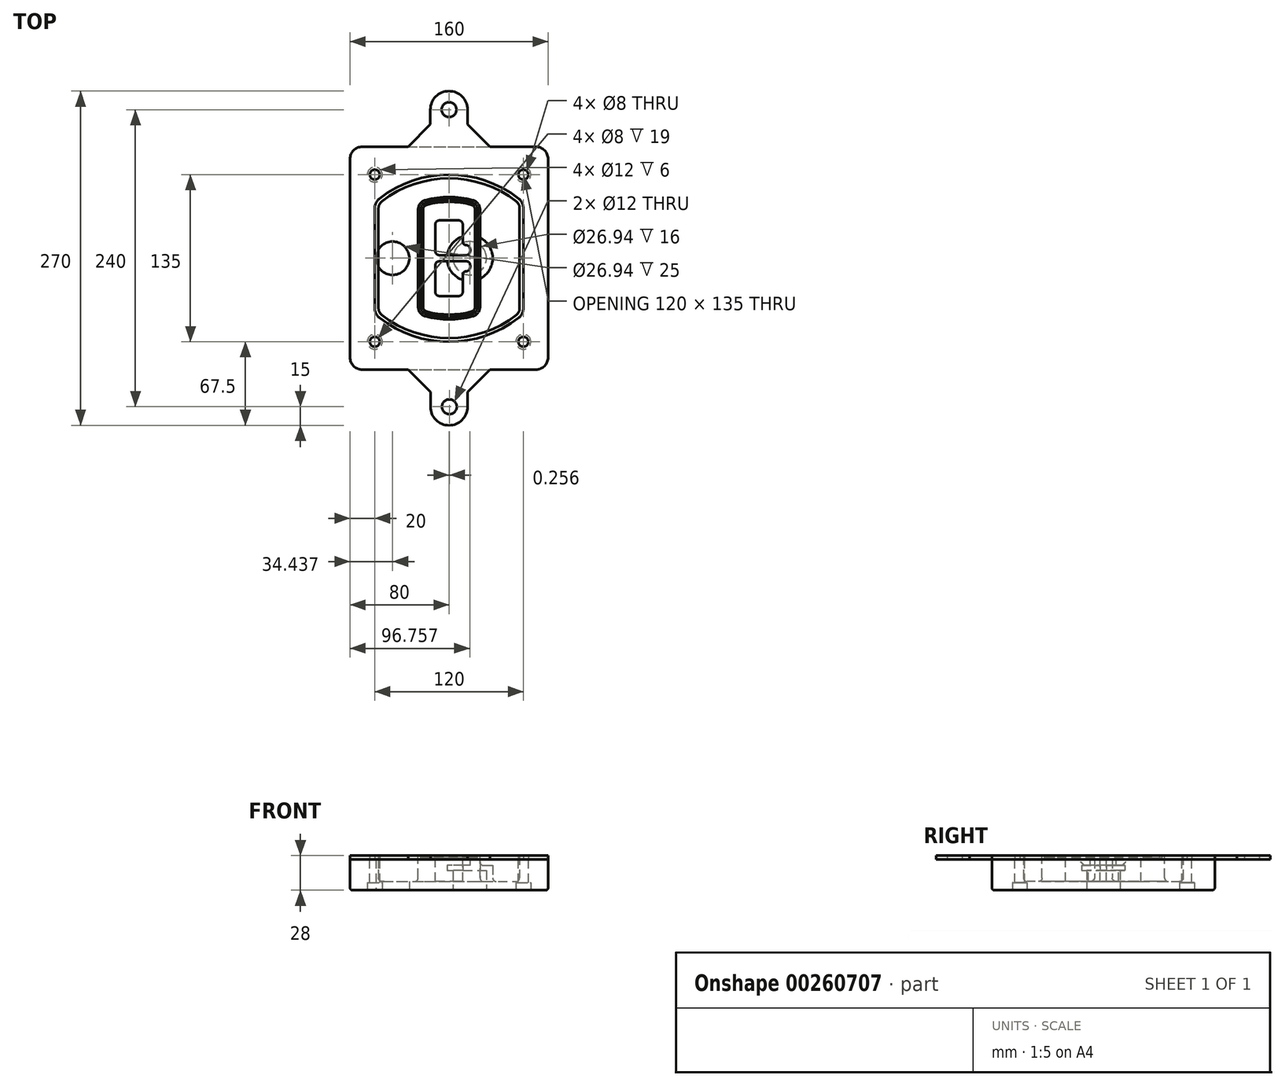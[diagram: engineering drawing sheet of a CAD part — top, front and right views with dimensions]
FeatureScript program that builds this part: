
annotation { "Feature Type Name" : "Feature", "Feature Type Description" : "" }
export const myFeature = defineFeature(function(context is Context, id is Id, definition is map)
    precondition{}
    {
        {
            var Q0;
            Q0=qCreatedBy(makeId("Top.planeOp"),FACE);
            var sketch = newSketch(context, id + "F0", { "sketchPlane" : qUnion([Q0])});
            skPoint(sketch, "E0.rect.middle", {"position": v(0, 0) * mm});
            skLineSegment(sketch, "E1.bottom", {"start": v(-70, -90) * mm, "end": v(70, -90) * mm});
            skLineSegment(sketch, "E1.top", {"start": v(-70, 90) * mm, "end": v(70, 90) * mm});
            skLineSegment(sketch, "E1.left", {"start": v(-80, -80) * mm, "end": v(-80, 80) * mm});
            skLineSegment(sketch, "E1.right", {"start": v(80, -80) * mm, "end": v(80, 80) * mm});
            skLineSegment(sketch, "E2", {"start": v(-80, 90) * mm, "end": v(80, -90) * mm, "construction": true});
            skLineSegment(sketch, "E3", {"start": v(80, 90) * mm, "end": v(-80, -90) * mm, "construction": true});
            skCircle(sketch, "E4", {"center": v(-60, 67.5) * mm, "radius": 4 * mm});
            skCircle(sketch, "E5", {"center": v(60, 67.5) * mm, "radius": 4 * mm});
            skCircle(sketch, "E6", {"center": v(60, -67.5) * mm, "radius": 4 * mm});
            skCircle(sketch, "E7", {"center": v(-60, -67.5) * mm, "radius": 4 * mm});
            skLineSegment(sketch, "E8", {"start": v(-60, 67.5) * mm, "end": v(60, 67.5) * mm, "construction": true});
            skLineSegment(sketch, "E9", {"start": v(60, 67.5) * mm, "end": v(60, -67.5) * mm, "construction": true});
            skLineSegment(sketch, "E10", {"start": v(60, -67.5) * mm, "end": v(-60, -67.5) * mm, "construction": true});
            skLineSegment(sketch, "E11", {"start": v(-60, -67.5) * mm, "end": v(-60, 67.5) * mm, "construction": true});
            skLineSegment(sketch, "E12", {"start": v(-60, 40.3) * mm, "end": v(-60, -40.3) * mm});
            skLineSegment(sketch, "E13", {"start": v(60, 40.3) * mm, "end": v(60, -40.3) * mm});
            skArc(sketch, "E14", {"start": v(56.15, 48.18) * mm, "mid": v(0, 67.5) * mm, "end": v(-56.15, 48.18) * mm});
            skArc(sketch, "E15", {"start": v(-56.15, -48.18) * mm, "mid": v(0, -67.5) * mm, "end": v(56.15, -48.18) * mm});
            skLineSegment(sketch, "E16", {"start": v(-60, 0) * mm, "end": v(60, 0) * mm, "construction": true});
            skPoint(sketch, "E17.visualSharp", {"position": v(-60, -45) * mm});
            skArc(sketch, "E17.filletArc", {"start": v(-60, -40.3) * mm, "mid": v(-58.99, -44.68) * mm, "end": v(-56.15, -48.18) * mm});
            skPoint(sketch, "E18.visualSharp", {"position": v(-60, 45) * mm});
            skArc(sketch, "E18.filletArc", {"start": v(-56.15, 48.18) * mm, "mid": v(-58.99, 44.68) * mm, "end": v(-60, 40.3) * mm});
            skPoint(sketch, "E19.visualSharp", {"position": v(60, 45) * mm});
            skArc(sketch, "E19.filletArc", {"start": v(60, 40.3) * mm, "mid": v(58.99, 44.68) * mm, "end": v(56.15, 48.18) * mm});
            skPoint(sketch, "E20.visualSharp", {"position": v(60, -45) * mm});
            skArc(sketch, "E20.filletArc", {"start": v(56.15, -48.18) * mm, "mid": v(58.99, -44.68) * mm, "end": v(60, -40.3) * mm});
            skPoint(sketch, "E21.visualSharp", {"position": v(-80, 90) * mm});
            skArc(sketch, "E21.filletArc", {"start": v(-70, 90) * mm, "mid": v(-77.07, 87.07) * mm, "end": v(-80, 80) * mm});
            skPoint(sketch, "E22.visualSharp", {"position": v(80, 90) * mm});
            skArc(sketch, "E22.filletArc", {"start": v(80, 80) * mm, "mid": v(77.07, 87.07) * mm, "end": v(70, 90) * mm});
            skPoint(sketch, "E23.visualSharp", {"position": v(80, -90) * mm});
            skArc(sketch, "E23.filletArc", {"start": v(70, -90) * mm, "mid": v(77.07, -87.07) * mm, "end": v(80, -80) * mm});
            skPoint(sketch, "E24.visualSharp", {"position": v(-80, -90) * mm});
            skArc(sketch, "E24.filletArc", {"start": v(-80, -80) * mm, "mid": v(-77.07, -87.07) * mm, "end": v(-70, -90) * mm});
            skArc(sketch, "E25.0", {"start": v(57, 40.3) * mm, "mid": v(56.3, 43.36) * mm, "end": v(54.3, 45.81) * mm});
            skLineSegment(sketch, "E25.1", {"start": v(57, 40.3) * mm, "end": v(57, -40.3) * mm});
            skArc(sketch, "E25.2", {"start": v(54.3, -45.81) * mm, "mid": v(56.3, -43.36) * mm, "end": v(57, -40.3) * mm});
            skArc(sketch, "E25.3", {"start": v(-54.3, -45.81) * mm, "mid": v(0, -64.5) * mm, "end": v(54.3, -45.81) * mm});
            skArc(sketch, "E25.4", {"start": v(-57, -40.3) * mm, "mid": v(-56.3, -43.36) * mm, "end": v(-54.3, -45.81) * mm});
            skArc(sketch, "E25.5", {"start": v(54.3, 45.81) * mm, "mid": v(0, 64.5) * mm, "end": v(-54.3, 45.81) * mm});
            skLineSegment(sketch, "E25.6", {"start": v(-57, 40.3) * mm, "end": v(-57, -40.3) * mm});
            skArc(sketch, "E25.7", {"start": v(-54.3, 45.81) * mm, "mid": v(-56.3, 43.36) * mm, "end": v(-57, 40.3) * mm});
            skArc(sketch, "E26.0", {"start": v(-58.62, 51.33) * mm, "mid": v(-62.58, 46.43) * mm, "end": v(-64, 40.3) * mm});
            skArc(sketch, "E26.1", {"start": v(58.62, 51.33) * mm, "mid": v(0, 71.5) * mm, "end": v(-58.62, 51.33) * mm});
            skArc(sketch, "E26.2", {"start": v(64, 40.3) * mm, "mid": v(62.58, 46.43) * mm, "end": v(58.62, 51.33) * mm});
            skLineSegment(sketch, "E26.3", {"start": v(64, 40.3) * mm, "end": v(64, -40.3) * mm});
            skArc(sketch, "E26.4", {"start": v(58.62, -51.33) * mm, "mid": v(62.58, -46.43) * mm, "end": v(64, -40.3) * mm});
            skLineSegment(sketch, "E26.5", {"start": v(-64, 40.3) * mm, "end": v(-64, -40.3) * mm});
            skArc(sketch, "E26.6", {"start": v(-58.62, -51.33) * mm, "mid": v(0, -71.5) * mm, "end": v(58.62, -51.33) * mm});
            skArc(sketch, "E26.7", {"start": v(-64, -40.3) * mm, "mid": v(-62.58, -46.43) * mm, "end": v(-58.62, -51.33) * mm});
            skSolve(sketch);
        }
        {
            var Q0;
            Q0=makeQuery(id+"F0.imprint","IMPRINT",FACE,{"disambiguationData":[TD([[makeQuery(id+"F0.imprint","IMPRINT",EDGE,{"derivedFrom":sQuery(id+"F0.wireOp",EDGE,"E1.bottom")}),1.0]])]});
            var Q1;
            Q1=makeQuery(id+"F0.imprint","IMPRINT",FACE,{"disambiguationData":[TD([[makeQuery(id+"F0.imprint","IMPRINT",EDGE,{"derivedFrom":sQuery(id+"F0.wireOp",EDGE,"E12")}),1.0]])]});
            var Q2;
            Q2=makeQuery(id+"F0.imprint","IMPRINT",FACE,{"disambiguationData":[TD([[makeQuery(id+"F0.imprint","IMPRINT",EDGE,{"derivedFrom":sQuery(id+"F0.wireOp",EDGE,"E25.0")}),1.0]])]});
            var Q3;
            Q3=makeQuery(id+"F0.imprint","IMPRINT",FACE,{"disambiguationData":[TD([[makeQuery(id+"F0.imprint","IMPRINT",EDGE,{"derivedFrom":sQuery(id+"F0.wireOp",EDGE,"E12")}),-1.0]])]});
            extrude(context, id + "F1", {"entities" : qUnion([Q0, Q1, Q2, Q3]), "oppositeDirection" : true, "depth" : 25 * mm});
        }
        {
            var Q0;
            Q0=makeQuery(id+"F0.imprint","IMPRINT",FACE,{"disambiguationData":[TD([[makeQuery(id+"F0.imprint","IMPRINT",EDGE,{"derivedFrom":sQuery(id+"F0.wireOp",EDGE,"E12")}),1.0]])]});
            extrude(context, id + "F2", {"entities" : qUnion([Q0]), "operationType" : NewBodyOperationType.ADD, "depth" : 3 * mm});
        }
        {
            var Q0;
            Q0=makeQuery(id+"F0.imprint","IMPRINT",FACE,{"disambiguationData":[TD([[makeQuery(id+"F0.imprint","IMPRINT",EDGE,{"derivedFrom":sQuery(id+"F0.wireOp",EDGE,"E25.0")}),1.0]])]});
            extrude(context, id + "F3", {"entities" : qUnion([Q0]), "operationType" : NewBodyOperationType.REMOVE, "oppositeDirection" : true, "depth" : 18 * mm});
        }
        {
            var Q0;
            Q0=makeQuery(id+"F2.opExtrude","CAP_FACE",FACE,{"disambiguationData":[OSD([sQuery(id+"F0.wireOp",EDGE,"E12"),sQuery(id+"F0.wireOp",EDGE,"E13"),sQuery(id+"F0.wireOp",EDGE,"E14"),sQuery(id+"F0.wireOp",EDGE,"E15"),sQuery(id+"F0.wireOp",EDGE,"E17.filletArc"),sQuery(id+"F0.wireOp",EDGE,"E18.filletArc"),sQuery(id+"F0.wireOp",EDGE,"E19.filletArc"),sQuery(id+"F0.wireOp",EDGE,"E20.filletArc"),sQuery(id+"F0.wireOp",EDGE,"E25.0"),sQuery(id+"F0.wireOp",EDGE,"E25.1"),sQuery(id+"F0.wireOp",EDGE,"E25.2"),sQuery(id+"F0.wireOp",EDGE,"E25.3"),sQuery(id+"F0.wireOp",EDGE,"E25.4"),sQuery(id+"F0.wireOp",EDGE,"E25.5"),sQuery(id+"F0.wireOp",EDGE,"E25.6"),sQuery(id+"F0.wireOp",EDGE,"E25.7")])],"isStart":false});
            var sketch = newSketch(context, id + "F4", { "sketchPlane" : qUnion([Q0])});
            skArc(sketch, "E27.0", {"start": v(-19.08, -46.97) * mm, "mid": v(0, -49.5) * mm, "end": v(19.08, -46.97) * mm});
            skArc(sketch, "E28.0", {"start": v(19.08, 46.97) * mm, "mid": v(0, 49.5) * mm, "end": v(-19.08, 46.97) * mm});
            skLineSegment(sketch, "E29", {"start": v(-25, 39.25) * mm, "end": v(-25, -39.25) * mm});
            skLineSegment(sketch, "E30", {"start": v(25, 39.25) * mm, "end": v(25, -39.25) * mm});
            skLineSegment(sketch, "E31", {"start": v(-25, 45.1) * mm, "end": v(25, 45.1) * mm, "construction": true});
            skLineSegment(sketch, "E32", {"start": v(-25, -45.1) * mm, "end": v(25, -45.1) * mm, "construction": true});
            skPoint(sketch, "E33.visualSharp", {"position": v(-25, 45.1) * mm});
            skArc(sketch, "E33.filletArc", {"start": v(-19.08, 46.97) * mm, "mid": v(-23.35, 44.11) * mm, "end": v(-25, 39.25) * mm});
            skPoint(sketch, "E34.visualSharp", {"position": v(25, 45.1) * mm});
            skArc(sketch, "E34.filletArc", {"start": v(25, 39.25) * mm, "mid": v(23.35, 44.11) * mm, "end": v(19.08, 46.97) * mm});
            skPoint(sketch, "E35.visualSharp", {"position": v(25, -45.1) * mm});
            skArc(sketch, "E35.filletArc", {"start": v(19.08, -46.97) * mm, "mid": v(23.35, -44.11) * mm, "end": v(25, -39.25) * mm});
            skPoint(sketch, "E36.visualSharp", {"position": v(-25, -45.1) * mm});
            skArc(sketch, "E36.filletArc", {"start": v(-25, -39.25) * mm, "mid": v(-23.35, -44.11) * mm, "end": v(-19.08, -46.97) * mm});
            skArc(sketch, "E37.0", {"start": v(54.3, 45.81) * mm, "mid": v(0, 64.5) * mm, "end": v(-54.3, 45.81) * mm});
            skArc(sketch, "E37.1", {"start": v(-54.3, 45.81) * mm, "mid": v(-56.3, 43.36) * mm, "end": v(-57, 40.3) * mm});
            skLineSegment(sketch, "E37.2", {"start": v(-57, 40.3) * mm, "end": v(-57, -40.3) * mm});
            skArc(sketch, "E37.3", {"start": v(-57, -40.3) * mm, "mid": v(-56.3, -43.36) * mm, "end": v(-54.3, -45.81) * mm});
            skArc(sketch, "E37.4", {"start": v(-54.3, -45.81) * mm, "mid": v(0, -64.5) * mm, "end": v(54.3, -45.81) * mm});
            skArc(sketch, "E37.5", {"start": v(54.3, -45.81) * mm, "mid": v(56.3, -43.36) * mm, "end": v(57, -40.3) * mm});
            skLineSegment(sketch, "E37.6", {"start": v(57, 40.3) * mm, "end": v(57, -40.3) * mm});
            skArc(sketch, "E37.7", {"start": v(57, 40.3) * mm, "mid": v(56.3, 43.36) * mm, "end": v(54.3, 45.81) * mm});
            skLineSegment(sketch, "E38.0", {"start": v(23, 39.25) * mm, "end": v(23, -39.25) * mm});
            skArc(sketch, "E38.1", {"start": v(18.56, -45.04) * mm, "mid": v(21.76, -42.9) * mm, "end": v(23, -39.25) * mm});
            skArc(sketch, "E38.2", {"start": v(-18.56, -45.04) * mm, "mid": v(0, -47.5) * mm, "end": v(18.56, -45.04) * mm});
            skArc(sketch, "E38.3", {"start": v(-23, -39.25) * mm, "mid": v(-21.76, -42.9) * mm, "end": v(-18.56, -45.04) * mm});
            skLineSegment(sketch, "E38.4", {"start": v(-23, 39.25) * mm, "end": v(-23, -39.25) * mm});
            skArc(sketch, "E38.5", {"start": v(23, 39.25) * mm, "mid": v(21.76, 42.9) * mm, "end": v(18.56, 45.04) * mm});
            skArc(sketch, "E38.6", {"start": v(-18.56, 45.04) * mm, "mid": v(-21.76, 42.9) * mm, "end": v(-23, 39.25) * mm});
            skArc(sketch, "E38.7", {"start": v(18.56, 45.04) * mm, "mid": v(0, 47.5) * mm, "end": v(-18.56, 45.04) * mm});
            skArc(sketch, "E39.0", {"start": v(21, 39.25) * mm, "mid": v(20.18, 41.68) * mm, "end": v(18.04, 43.1) * mm});
            skLineSegment(sketch, "E39.1", {"start": v(21, 39.25) * mm, "end": v(21, -39.25) * mm});
            skArc(sketch, "E39.2", {"start": v(18.04, -43.1) * mm, "mid": v(20.18, -41.68) * mm, "end": v(21, -39.25) * mm});
            skArc(sketch, "E39.3", {"start": v(-18.04, -43.1) * mm, "mid": v(0, -45.5) * mm, "end": v(18.04, -43.1) * mm});
            skArc(sketch, "E39.4", {"start": v(-21, -39.25) * mm, "mid": v(-20.18, -41.68) * mm, "end": v(-18.04, -43.1) * mm});
            skArc(sketch, "E39.5", {"start": v(18.04, 43.1) * mm, "mid": v(0, 45.5) * mm, "end": v(-18.04, 43.1) * mm});
            skLineSegment(sketch, "E39.6", {"start": v(-21, 39.25) * mm, "end": v(-21, -39.25) * mm});
            skArc(sketch, "E39.7", {"start": v(-18.04, 43.1) * mm, "mid": v(-20.18, 41.68) * mm, "end": v(-21, 39.25) * mm});
            skLineSegment(sketch, "E40", {"start": v(-25, 0) * mm, "end": v(25, 0) * mm, "construction": true});
            skLineSegment(sketch, "E41", {"start": v(-11, 5.5) * mm, "end": v(-11, 27.5) * mm});
            skLineSegment(sketch, "E42", {"start": v(-8, 30.5) * mm, "end": v(8, 30.5) * mm});
            skLineSegment(sketch, "E43", {"start": v(11, 27.5) * mm, "end": v(11, 13.5) * mm});
            skLineSegment(sketch, "E44", {"start": v(14, 10.5) * mm, "end": v(14, 10.5) * mm});
            skLineSegment(sketch, "E45", {"start": v(17, 7.5) * mm, "end": v(17, 5.5) * mm});
            skLineSegment(sketch, "E46", {"start": v(14, 2.5) * mm, "end": v(-8, 2.5) * mm});
            skPoint(sketch, "E47.visualSharp", {"position": v(-11, 30.5) * mm});
            skArc(sketch, "E47.filletArc", {"start": v(-8, 30.5) * mm, "mid": v(-10.12, 29.62) * mm, "end": v(-11, 27.5) * mm});
            skPoint(sketch, "E48.visualSharp", {"position": v(11, 30.5) * mm});
            skArc(sketch, "E48.filletArc", {"start": v(11, 27.5) * mm, "mid": v(10.12, 29.62) * mm, "end": v(8, 30.5) * mm});
            skPoint(sketch, "E49.visualSharp", {"position": v(11, 10.5) * mm});
            skArc(sketch, "E49.filletArc", {"start": v(11, 13.5) * mm, "mid": v(11.88, 11.38) * mm, "end": v(14, 10.5) * mm});
            skPoint(sketch, "E50.visualSharp", {"position": v(17, 10.5) * mm});
            skArc(sketch, "E50.filletArc", {"start": v(17, 7.5) * mm, "mid": v(16.12, 9.62) * mm, "end": v(14, 10.5) * mm});
            skPoint(sketch, "E51.visualSharp", {"position": v(17, 2.5) * mm});
            skArc(sketch, "E51.filletArc", {"start": v(14, 2.5) * mm, "mid": v(16.12, 3.38) * mm, "end": v(17, 5.5) * mm});
            skPoint(sketch, "E52.visualSharp", {"position": v(-11, 2.5) * mm});
            skArc(sketch, "E52.filletArc", {"start": v(-11, 5.5) * mm, "mid": v(-10.12, 3.38) * mm, "end": v(-8, 2.5) * mm});
            skLineSegment(sketch, "E53.0.MirrorCS", {"start": v(14, -2.5) * mm, "end": v(-8, -2.5) * mm});
            skArc(sketch, "E54.0.MirrorCS", {"start": v(-11, -5.5) * mm, "mid": v(-10.12, -3.38) * mm, "end": v(-8, -2.5) * mm});
            skLineSegment(sketch, "E55.0.MirrorCS", {"start": v(-11, -5.5) * mm, "end": v(-11, -27.5) * mm});
            skArc(sketch, "E56.0.MirrorCS", {"start": v(-8, -30.5) * mm, "mid": v(-10.12, -29.62) * mm, "end": v(-11, -27.5) * mm});
            skLineSegment(sketch, "E57.0.MirrorCS", {"start": v(-8, -30.5) * mm, "end": v(8, -30.5) * mm});
            skArc(sketch, "E58.0.MirrorCS", {"start": v(11, -27.5) * mm, "mid": v(10.12, -29.62) * mm, "end": v(8, -30.5) * mm});
            skLineSegment(sketch, "E59.0.MirrorCS", {"start": v(11, -27.5) * mm, "end": v(11, -13.5) * mm});
            skArc(sketch, "E60.0.MirrorCS", {"start": v(11, -13.5) * mm, "mid": v(11.88, -11.38) * mm, "end": v(14, -10.5) * mm});
            skArc(sketch, "E61.0.MirrorCS", {"start": v(17, -7.5) * mm, "mid": v(16.12, -9.62) * mm, "end": v(14, -10.5) * mm});
            skLineSegment(sketch, "E62.0.MirrorCS", {"start": v(17, -7.5) * mm, "end": v(17, -5.5) * mm});
            skArc(sketch, "E63.0.MirrorCS", {"start": v(14, -2.5) * mm, "mid": v(16.12, -3.38) * mm, "end": v(17, -5.5) * mm});
            skSolve(sketch);
        }
        {
            var Q0;
            Q0=makeQuery(id+"F4.imprint","IMPRINT",FACE,{"disambiguationData":[TD([[makeQuery(id+"F4.imprint","IMPRINT",EDGE,{"derivedFrom":sQuery(id+"F4.wireOp",EDGE,"E27.0")}),1.0]])]});
            var Q1;
            Q1=makeQuery(id+"F4.imprint","IMPRINT",FACE,{"disambiguationData":[TD([[makeQuery(id+"F4.imprint","IMPRINT",EDGE,{"derivedFrom":sQuery(id+"F4.wireOp",EDGE,"E38.0")}),-1.0]])]});
            var Q2;
            Q2=makeQuery(id+"F4.imprint","IMPRINT",FACE,{"disambiguationData":[TD([[makeQuery(id+"F4.imprint","IMPRINT",EDGE,{"derivedFrom":sQuery(id+"F4.wireOp",EDGE,"E39.0")}),1.0]])]});
            extrude(context, id + "F5", {"entities" : qUnion([Q0, Q1, Q2]), "operationType" : NewBodyOperationType.ADD, "endBound" : BoundingType.UP_TO_NEXT, "oppositeDirection" : true, "depth" : 25 * mm});
        }
        {
            var Q0;
            Q0=makeQuery(id+"F4.imprint","IMPRINT",FACE,{"disambiguationData":[TD([[makeQuery(id+"F4.imprint","IMPRINT",EDGE,{"derivedFrom":sQuery(id+"F4.wireOp",EDGE,"E38.0")}),-1.0]])]});
            extrude(context, id + "F6", {"entities" : qUnion([Q0]), "operationType" : NewBodyOperationType.REMOVE, "oppositeDirection" : true, "depth" : 2 * mm});
        }
        {
            var Q0;
            Q0=makeQuery(id+"F1.opExtrude","CAP_FACE",FACE,{"disambiguationData":[OSD([sQuery(id+"F0.wireOp",EDGE,"E1.bottom"),sQuery(id+"F0.wireOp",EDGE,"E1.top"),sQuery(id+"F0.wireOp",EDGE,"E1.left"),sQuery(id+"F0.wireOp",EDGE,"E1.right"),sQuery(id+"F0.wireOp",EDGE,"E4"),sQuery(id+"F0.wireOp",EDGE,"E5"),sQuery(id+"F0.wireOp",EDGE,"E6"),sQuery(id+"F0.wireOp",EDGE,"E7"),sQuery(id+"F0.wireOp",EDGE,"E21.filletArc"),sQuery(id+"F0.wireOp",EDGE,"E22.filletArc"),sQuery(id+"F0.wireOp",EDGE,"E23.filletArc"),sQuery(id+"F0.wireOp",EDGE,"E24.filletArc")])],"isStart":false});
            var sketch = newSketch(context, id + "F7", { "sketchPlane" : qUnion([Q0])});
            skCircle(sketch, "E64", {"center": v(16.76, 0) * mm, "radius": 13.47 * mm});
            skCircle(sketch, "E65", {"center": v(-45.56, 0) * mm, "radius": 13.47 * mm});
            skLineSegment(sketch, "E66", {"start": v(80, 0) * mm, "end": v(-80, 0) * mm});
            skCircle(sketch, "E67", {"center": v(16.76, 0) * mm, "radius": 18.47 * mm});
            skCircle(sketch, "E68", {"center": v(60, -67.5) * mm, "radius": 6 * mm});
            skCircle(sketch, "E69", {"center": v(-60, -67.5) * mm, "radius": 6 * mm});
            skCircle(sketch, "E70", {"center": v(-60, 67.5) * mm, "radius": 6 * mm});
            skCircle(sketch, "E71", {"center": v(60, 67.5) * mm, "radius": 6 * mm});
            skSolve(sketch);
        }
        {
            var Q0;
            {var subQ1=sQuery(id+"F7.wireOp",EDGE,"E66");var subQ4=sQuery(id+"F7.wireOp",EDGE,"E64");var subQ6=makeQuery(id+"F7.imprint","INTERSECT",VERTEX,{"disambiguationData":[OD(0.0)],"derivedFrom":[subQ4,subQ1]});Q0=makeQuery(id+"F7.imprint","IMPRINT",FACE,{"disambiguationData":[TD([[makeQuery(id+"F7.imprint","IMPRINT",EDGE,{"disambiguationData":[TD([[subQ6,-1.0]])],"derivedFrom":subQ4}),-1.0]])]});}
            var Q1;
            {var subQ0=sQuery(id+"F7.wireOp",EDGE,"E66");var subQ1=sQuery(id+"F7.wireOp",EDGE,"E64");var subQ3=makeQuery(id+"F7.imprint","INTERSECT",VERTEX,{"disambiguationData":[OD(0.0)],"derivedFrom":[subQ1,subQ0]});Q1=makeQuery(id+"F7.imprint","IMPRINT",FACE,{"disambiguationData":[TD([[makeQuery(id+"F7.imprint","IMPRINT",EDGE,{"disambiguationData":[TD([[subQ3,-1.0]])],"derivedFrom":subQ1}),1.0]])]});}
            var Q2;
            {var subQ0=sQuery(id+"F7.wireOp",EDGE,"E66");var subQ1=sQuery(id+"F7.wireOp",EDGE,"E64");var subQ3=makeQuery(id+"F7.imprint","INTERSECT",VERTEX,{"disambiguationData":[OD(0.0)],"derivedFrom":[subQ1,subQ0]});Q2=makeQuery(id+"F7.imprint","IMPRINT",FACE,{"disambiguationData":[TD([[makeQuery(id+"F7.imprint","IMPRINT",EDGE,{"disambiguationData":[TD([[subQ3,1.0]])],"derivedFrom":subQ1}),1.0]])]});}
            var Q3;
            {var subQ1=sQuery(id+"F7.wireOp",EDGE,"E66");var subQ4=sQuery(id+"F7.wireOp",EDGE,"E64");var subQ6=makeQuery(id+"F7.imprint","INTERSECT",VERTEX,{"disambiguationData":[OD(0.0)],"derivedFrom":[subQ4,subQ1]});Q3=makeQuery(id+"F7.imprint","IMPRINT",FACE,{"disambiguationData":[TD([[makeQuery(id+"F7.imprint","IMPRINT",EDGE,{"disambiguationData":[TD([[subQ6,1.0]])],"derivedFrom":subQ4}),-1.0]])]});}
            extrude(context, id + "F8", {"entities" : qUnion([Q0, Q1, Q2, Q3]), "operationType" : NewBodyOperationType.ADD, "oppositeDirection" : true, "depth" : 20 * mm});
        }
        {
            var Q0;
            {var subQ0=sQuery(id+"F7.wireOp",EDGE,"E66");var subQ1=sQuery(id+"F7.wireOp",EDGE,"E64");var subQ3=makeQuery(id+"F7.imprint","INTERSECT",VERTEX,{"disambiguationData":[OD(0.0)],"derivedFrom":[subQ1,subQ0]});Q0=makeQuery(id+"F7.imprint","IMPRINT",FACE,{"disambiguationData":[TD([[makeQuery(id+"F7.imprint","IMPRINT",EDGE,{"disambiguationData":[TD([[subQ3,-1.0]])],"derivedFrom":subQ1}),1.0]])]});}
            var Q1;
            {var subQ0=sQuery(id+"F7.wireOp",EDGE,"E66");var subQ1=sQuery(id+"F7.wireOp",EDGE,"E64");var subQ3=makeQuery(id+"F7.imprint","INTERSECT",VERTEX,{"disambiguationData":[OD(0.0)],"derivedFrom":[subQ1,subQ0]});Q1=makeQuery(id+"F7.imprint","IMPRINT",FACE,{"disambiguationData":[TD([[makeQuery(id+"F7.imprint","IMPRINT",EDGE,{"disambiguationData":[TD([[subQ3,1.0]])],"derivedFrom":subQ1}),1.0]])]});}
            extrude(context, id + "F9", {"entities" : qUnion([Q0, Q1]), "operationType" : NewBodyOperationType.REMOVE, "oppositeDirection" : true, "depth" : 16 * mm});
        }
        {
            var Q0;
            {var subQ0=sQuery(id+"F7.wireOp",EDGE,"E66");var subQ1=sQuery(id+"F7.wireOp",EDGE,"E65");var subQ3=makeQuery(id+"F7.imprint","INTERSECT",VERTEX,{"disambiguationData":[OD(0.0)],"derivedFrom":[subQ1,subQ0]});Q0=makeQuery(id+"F7.imprint","IMPRINT",FACE,{"disambiguationData":[TD([[makeQuery(id+"F7.imprint","IMPRINT",EDGE,{"disambiguationData":[TD([[subQ3,-1.0]])],"derivedFrom":subQ1}),1.0]])]});}
            var Q1;
            {var subQ0=sQuery(id+"F7.wireOp",EDGE,"E66");var subQ1=sQuery(id+"F7.wireOp",EDGE,"E65");var subQ3=makeQuery(id+"F7.imprint","INTERSECT",VERTEX,{"disambiguationData":[OD(0.0)],"derivedFrom":[subQ1,subQ0]});Q1=makeQuery(id+"F7.imprint","IMPRINT",FACE,{"disambiguationData":[TD([[makeQuery(id+"F7.imprint","IMPRINT",EDGE,{"disambiguationData":[TD([[subQ3,1.0]])],"derivedFrom":subQ1}),1.0]])]});}
            extrude(context, id + "F10", {"entities" : qUnion([Q0, Q1]), "operationType" : NewBodyOperationType.REMOVE, "oppositeDirection" : true, "depth" : 25 * mm});
        }
        {
            var Q0;
            Q0=makeQuery(id+"F7.imprint","IMPRINT",FACE,{"disambiguationData":[TD([[makeQuery(id+"F7.imprint","IMPRINT",EDGE,{"derivedFrom":sQuery(id+"F7.wireOp",EDGE,"E68")}),1.0]])]});
            var Q1;
            Q1=makeQuery(id+"F7.imprint","IMPRINT",FACE,{"disambiguationData":[TD([[makeQuery(id+"F7.imprint","IMPRINT",EDGE,{"derivedFrom":makeQuery(id+"F1.opExtrude","CAP_EDGE",EDGE,{"disambiguationData":[OSD([sQuery(id+"F0.wireOp",EDGE,"E5")])],"isStart":false})}),-1.0]])]});
            var Q2;
            Q2=makeQuery(id+"F7.imprint","IMPRINT",FACE,{"disambiguationData":[TD([[makeQuery(id+"F7.imprint","IMPRINT",EDGE,{"derivedFrom":sQuery(id+"F7.wireOp",EDGE,"E69")}),1.0]])]});
            var Q3;
            Q3=makeQuery(id+"F7.imprint","IMPRINT",FACE,{"disambiguationData":[TD([[makeQuery(id+"F7.imprint","IMPRINT",EDGE,{"derivedFrom":makeQuery(id+"F1.opExtrude","CAP_EDGE",EDGE,{"disambiguationData":[OSD([sQuery(id+"F0.wireOp",EDGE,"E4")])],"isStart":false})}),-1.0]])]});
            var Q4;
            Q4=makeQuery(id+"F7.imprint","IMPRINT",FACE,{"disambiguationData":[TD([[makeQuery(id+"F7.imprint","IMPRINT",EDGE,{"derivedFrom":sQuery(id+"F7.wireOp",EDGE,"E70")}),1.0]])]});
            var Q5;
            Q5=makeQuery(id+"F7.imprint","IMPRINT",FACE,{"disambiguationData":[TD([[makeQuery(id+"F7.imprint","IMPRINT",EDGE,{"derivedFrom":makeQuery(id+"F1.opExtrude","CAP_EDGE",EDGE,{"disambiguationData":[OSD([sQuery(id+"F0.wireOp",EDGE,"E7")])],"isStart":false})}),-1.0]])]});
            var Q6;
            Q6=makeQuery(id+"F7.imprint","IMPRINT",FACE,{"disambiguationData":[TD([[makeQuery(id+"F7.imprint","IMPRINT",EDGE,{"derivedFrom":sQuery(id+"F7.wireOp",EDGE,"E71")}),1.0]])]});
            var Q7;
            Q7=makeQuery(id+"F7.imprint","IMPRINT",FACE,{"disambiguationData":[TD([[makeQuery(id+"F7.imprint","IMPRINT",EDGE,{"derivedFrom":makeQuery(id+"F1.opExtrude","CAP_EDGE",EDGE,{"disambiguationData":[OSD([sQuery(id+"F0.wireOp",EDGE,"E6")])],"isStart":false})}),-1.0]])]});
            extrude(context, id + "F11", {"entities" : qUnion([Q0, Q1, Q2, Q3, Q4, Q5, Q6, Q7]), "operationType" : NewBodyOperationType.REMOVE, "oppositeDirection" : true, "depth" : 6 * mm});
        }
        {
            var Q0;
            Q0=makeQuery(id+"F9.boolean.opBoolean","COPY",FACE,{"derivedFrom":makeQuery(id+"F9.opExtrude","CAP_FACE",FACE,{"disambiguationData":[OSD([sQuery(id+"F7.wireOp",EDGE,"E64")])],"isStart":false})});
            var sketch = newSketch(context, id + "F12", { "sketchPlane" : qUnion([Q0])});
            skArc(sketch, "E72.0", {"start": v(11, 17.55) * mm, "mid": v(2.57, 11.82) * mm, "end": v(-1.54, 2.5) * mm});
            skArc(sketch, "E72.1", {"start": v(-1.54, -2.5) * mm, "mid": v(2.57, -11.82) * mm, "end": v(11, -17.55) * mm});
            skLineSegment(sketch, "E73", {"start": v(-1.54, -2.5) * mm, "end": v(14, -2.5) * mm});
            skLineSegment(sketch, "E74.0", {"start": v(14, 2.5) * mm, "end": v(-1.54, 2.5) * mm});
            skArc(sketch, "E74.1", {"start": v(14, 2.5) * mm, "mid": v(16.12, 3.38) * mm, "end": v(17, 5.5) * mm});
            skLineSegment(sketch, "E74.2", {"start": v(17, 7.5) * mm, "end": v(17, 5.5) * mm});
            skArc(sketch, "E74.3", {"start": v(17, 7.5) * mm, "mid": v(16.12, 9.62) * mm, "end": v(14, 10.5) * mm});
            skArc(sketch, "E74.4", {"start": v(11, 13.5) * mm, "mid": v(11.88, 11.38) * mm, "end": v(14, 10.5) * mm});
            skLineSegment(sketch, "E74.5", {"start": v(11, 17.55) * mm, "end": v(11, 13.5) * mm});
            skLineSegment(sketch, "E74.7", {"start": v(14, -2.5) * mm, "end": v(-1.54, -2.5) * mm});
            skArc(sketch, "E74.8", {"start": v(14, -2.5) * mm, "mid": v(16.12, -3.38) * mm, "end": v(17, -5.5) * mm});
            skLineSegment(sketch, "E74.9", {"start": v(17, -7.5) * mm, "end": v(17, -5.5) * mm});
            skArc(sketch, "E74.10", {"start": v(17, -7.5) * mm, "mid": v(16.12, -9.62) * mm, "end": v(14, -10.5) * mm});
            skArc(sketch, "E74.11", {"start": v(11, -13.5) * mm, "mid": v(11.88, -11.38) * mm, "end": v(14, -10.5) * mm});
            skLineSegment(sketch, "E74.12", {"start": v(11, -17.55) * mm, "end": v(11, -13.5) * mm});
            skPoint(sketch, "E75.orphan", {"position": v(11, -27.5) * mm});
            skPoint(sketch, "E76.orphan", {"position": v(-8, -2.5) * mm});
            skPoint(sketch, "E77.orphan", {"position": v(-8, 2.5) * mm});
            skPoint(sketch, "E78.orphan", {"position": v(11, 27.5) * mm});
            skSolve(sketch);
        }
        {
            var Q0;
            {var subQ7=sQuery(id+"F12.wireOp",EDGE,"E72.0");var subQ14=sQuery(id+"F12.wireOp",EDGE,"E72.1");var subQ16=sQuery(id+"F12.wireOp",EDGE,"E74.1");var subQ18=sQuery(id+"F12.wireOp",EDGE,"E74.8");Q0=qUnion([makeQuery(id+"F12.imprint","IMPRINT",FACE,{"disambiguationData":[TD([[makeQuery(id+"F12.imprint","IMPRINT",EDGE,{"derivedFrom":subQ7}),1.0]])]}),makeQuery(id+"F12.imprint","IMPRINT",FACE,{"disambiguationData":[TD([[makeQuery(id+"F12.imprint","IMPRINT",EDGE,{"derivedFrom":subQ14}),1.0]])]}),makeQuery(id+"F12.imprint","IMPRINT",FACE,{"disambiguationData":[TD([[makeQuery(id+"F12.imprint","IMPRINT",EDGE,{"derivedFrom":subQ16}),1.0]])]}),makeQuery(id+"F12.imprint","IMPRINT",FACE,{"disambiguationData":[TD([[makeQuery(id+"F12.imprint","IMPRINT",EDGE,{"derivedFrom":subQ18}),-1.0]])]})]);}
            var Q1;
            Q1=makeQuery(id+"F5.boolean.opBoolean","SPLIT",FACE,{"disambiguationData":[TD([makeQuery(id+"F5.opExtrude","SWEPT_FACE",FACE,{"disambiguationData":[OSD([sQuery(id+"F4.wireOp",EDGE,"E41")])]})])],"derivedFrom":makeQuery(id+"F3.boolean.opBoolean","COPY",FACE,{"derivedFrom":makeQuery(id+"F3.opExtrude","CAP_FACE",FACE,{"disambiguationData":[OSD([sQuery(id+"F0.wireOp",EDGE,"E25.0"),sQuery(id+"F0.wireOp",EDGE,"E25.1"),sQuery(id+"F0.wireOp",EDGE,"E25.2"),sQuery(id+"F0.wireOp",EDGE,"E25.3"),sQuery(id+"F0.wireOp",EDGE,"E25.4"),sQuery(id+"F0.wireOp",EDGE,"E25.5"),sQuery(id+"F0.wireOp",EDGE,"E25.6"),sQuery(id+"F0.wireOp",EDGE,"E25.7")])],"isStart":false})})});
            extrude(context, id + "F13", {"entities" : qUnion([Q0]), "operationType" : NewBodyOperationType.REMOVE, "endBound" : BoundingType.UP_TO_SURFACE, "endBoundEntityFace" : qUnion([Q1]), "depth" : 25 * mm});
        }
        {
            var Q0;
            Q0=makeQuery(id+"F3.boolean.opBoolean","COPY",EDGE,{"derivedFrom":makeQuery(id+"F3.opExtrude","CAP_EDGE",EDGE,{"disambiguationData":[OSD([sQuery(id+"F0.wireOp",EDGE,"E25.6")])],"isStart":false})});
            var Q1;
            Q1=makeQuery(id+"F8.boolean.opBoolean","INTERSECT",EDGE,{"derivedFrom":[makeQuery(id+"F5.opExtrude","SWEPT_FACE",FACE,{"disambiguationData":[OSD([sQuery(id+"F4.wireOp",EDGE,"E30")])]}),makeQuery(id+"F8.opExtrude","CAP_FACE",FACE,{"disambiguationData":[OSD([sQuery(id+"F7.wireOp",EDGE,"E67")])],"isStart":false})]});
            var Q2;
            Q2=makeQuery(id+"F8.boolean.opBoolean","INTERSECT",EDGE,{"disambiguationData":[OD(1.0)],"derivedFrom":[makeQuery(id+"F5.opExtrude","SWEPT_FACE",FACE,{"disambiguationData":[OSD([sQuery(id+"F4.wireOp",EDGE,"E30")])]}),makeQuery(id+"F8.opExtrude","SWEPT_FACE",FACE,{"disambiguationData":[OSD([sQuery(id+"F7.wireOp",EDGE,"E67")])]})]});
            var Q3;
            {var subQ0=sQuery(id+"F4.wireOp",EDGE,"E30");Q3=makeQuery(id+"F8.boolean.opBoolean","SPLIT",EDGE,{"disambiguationData":[TD([makeQuery(id+"F5.opExtrude","SWEPT_FACE",FACE,{"disambiguationData":[OSD([sQuery(id+"F4.wireOp",EDGE,"E35.filletArc")])]})])],"derivedFrom":makeQuery(id+"F5.opExtrude","CAP_EDGE",EDGE,{"disambiguationData":[OSD([subQ0])],"isStart":false})});}
            var Q4;
            {var subQ0=sQuery(id+"F0.wireOp",EDGE,"E25.7");var subQ1=sQuery(id+"F0.wireOp",EDGE,"E25.1");var subQ2=sQuery(id+"F0.wireOp",EDGE,"E25.6");var subQ3=sQuery(id+"F0.wireOp",EDGE,"E25.5");var subQ4=sQuery(id+"F0.wireOp",EDGE,"E25.4");var subQ5=sQuery(id+"F0.wireOp",EDGE,"E25.0");var subQ6=sQuery(id+"F0.wireOp",EDGE,"E25.2");var subQ7=sQuery(id+"F0.wireOp",EDGE,"E25.3");Q4=makeQuery(id+"F8.boolean.opBoolean","INTERSECT",EDGE,{"derivedFrom":[makeQuery(id+"F5.boolean.opBoolean","SPLIT",FACE,{"disambiguationData":[TD([makeQuery(id+"F2.opExtrude","SWEPT_FACE",FACE,{"disambiguationData":[OSD([subQ5])]})])],"derivedFrom":makeQuery(id+"F3.boolean.opBoolean","COPY",FACE,{"derivedFrom":makeQuery(id+"F3.opExtrude","CAP_FACE",FACE,{"disambiguationData":[OSD([subQ5,subQ1,subQ6,subQ7,subQ4,subQ3,subQ2,subQ0])],"isStart":false})})}),makeQuery(id+"F8.opExtrude","SWEPT_FACE",FACE,{"disambiguationData":[OSD([sQuery(id+"F7.wireOp",EDGE,"E67")])]})]});}
            var Q5;
            Q5=makeQuery(id+"F8.boolean.opBoolean","INTERSECT",EDGE,{"disambiguationData":[OD(0.0)],"derivedFrom":[makeQuery(id+"F5.opExtrude","SWEPT_FACE",FACE,{"disambiguationData":[OSD([sQuery(id+"F4.wireOp",EDGE,"E30")])]}),makeQuery(id+"F8.opExtrude","SWEPT_FACE",FACE,{"disambiguationData":[OSD([sQuery(id+"F7.wireOp",EDGE,"E67")])]})]});
            fillet(context, id + "F14", {"entities" : qUnion([Q0, Q1, Q2, Q3, Q4, Q5]), "radius" : 3 * mm, "tangentPropagation" : true, "allowEdgeOverflow" : false});
        }
        {
            var Q0;
            Q0=makeQuery(id+"F1.opExtrude","CAP_EDGE",EDGE,{"disambiguationData":[OSD([sQuery(id+"F0.wireOp",EDGE,"E1.bottom")])],"isStart":false});
            fillet(context, id + "F15", {"entities" : qUnion([Q0]), "radius" : 2 * mm, "tangentPropagation" : true, "allowEdgeOverflow" : false});
        }
        {
            var Q0;
            {var subQ0=sQuery(id+"F0.wireOp",EDGE,"E22.filletArc");var subQ1=sQuery(id+"F0.wireOp",EDGE,"E7");var subQ2=sQuery(id+"F0.wireOp",EDGE,"E6");var subQ3=sQuery(id+"F0.wireOp",EDGE,"E5");var subQ4=sQuery(id+"F0.wireOp",EDGE,"E4");var subQ5=sQuery(id+"F0.wireOp",EDGE,"E1.bottom");var subQ6=sQuery(id+"F0.wireOp",EDGE,"E21.filletArc");var subQ7=sQuery(id+"F0.wireOp",EDGE,"E1.top");var subQ8=sQuery(id+"F0.wireOp",EDGE,"E1.left");var subQ9=sQuery(id+"F0.wireOp",EDGE,"E1.right");var subQ10=sQuery(id+"F0.wireOp",EDGE,"E23.filletArc");var subQ11=sQuery(id+"F0.wireOp",EDGE,"E24.filletArc");Q0=makeQuery(id+"F2.boolean.opBoolean","SPLIT",FACE,{"disambiguationData":[TD([makeQuery(id+"F1.opExtrude","SWEPT_FACE",FACE,{"disambiguationData":[OSD([subQ5])]})])],"derivedFrom":makeQuery(id+"F1.opExtrude","CAP_FACE",FACE,{"disambiguationData":[OSD([subQ5,subQ7,subQ8,subQ9,subQ4,subQ3,subQ2,subQ1,subQ6,subQ0,subQ10,subQ11])],"isStart":true})});}
            var sketch = newSketch(context, id + "F16", { "sketchPlane" : qUnion([Q0])});
            skCircle(sketch, "E79", {"center": v(0, 120) * mm, "radius": 6 * mm});
            skArc(sketch, "E80", {"start": v(14.9, 120) * mm, "mid": v(-0.1, 135) * mm, "end": v(-15.1, 120) * mm});
            skLineSegment(sketch, "E81", {"start": v(-15.1, 120) * mm, "end": v(-15.1, 108) * mm});
            skLineSegment(sketch, "E82", {"start": v(14.9, 120) * mm, "end": v(14.9, 108) * mm});
            skLineSegment(sketch, "E83", {"start": v(-15.1, 108) * mm, "end": v(-33.1, 90) * mm});
            skLineSegment(sketch, "E84", {"start": v(14.9, 108) * mm, "end": v(32.9, 90) * mm});
            skCircle(sketch, "E85", {"center": v(0.26, -120) * mm, "radius": 6 * mm});
            skArc(sketch, "E86", {"start": v(-15, -120) * mm, "mid": v(0, -135) * mm, "end": v(15, -120) * mm});
            skLineSegment(sketch, "E87", {"start": v(15, -120) * mm, "end": v(15, -108) * mm});
            skLineSegment(sketch, "E88", {"start": v(-15, -120) * mm, "end": v(-15, -108) * mm});
            skLineSegment(sketch, "E89", {"start": v(15, -108) * mm, "end": v(33, -90) * mm});
            skLineSegment(sketch, "E90", {"start": v(-15, -108) * mm, "end": v(-33, -90) * mm});
            skLineSegment(sketch, "E91", {"start": v(-70, 90) * mm, "end": v(70, 90) * mm});
            skLineSegment(sketch, "E92", {"start": v(-80, 80) * mm, "end": v(-80, -80) * mm});
            skLineSegment(sketch, "E93", {"start": v(-70, -90) * mm, "end": v(70, -90) * mm});
            skLineSegment(sketch, "E94", {"start": v(80, -80) * mm, "end": v(80, 80) * mm});
            skArc(sketch, "E95", {"start": v(-70, 90) * mm, "mid": v(-77.07, 87.07) * mm, "end": v(-80, 80) * mm});
            skArc(sketch, "E96", {"start": v(70.06, -89.94) * mm, "mid": v(77.07, -87) * mm, "end": v(80, -80) * mm});
            skArc(sketch, "E97", {"start": v(-79.94, -80.06) * mm, "mid": v(-77, -87.07) * mm, "end": v(-70, -90) * mm});
            skArc(sketch, "E98", {"start": v(79.94, 80.06) * mm, "mid": v(77, 87.07) * mm, "end": v(70, 90) * mm});
            skCircle(sketch, "E99", {"center": v(-60, 67.5) * mm, "radius": 4 * mm});
            skCircle(sketch, "E100", {"center": v(60, 67.5) * mm, "radius": 4 * mm});
            skCircle(sketch, "E101", {"center": v(-60, -67.5) * mm, "radius": 4 * mm});
            skCircle(sketch, "E102", {"center": v(60, -67.5) * mm, "radius": 4 * mm});
            skPoint(sketch, "E103.endSnap0", {"position": v(0, -90) * mm});
            skSolve(sketch);
        }
        {
            var Q0;
            Q0=makeQuery(id+"F16.imprint","IMPRINT",FACE,{"disambiguationData":[TD([[makeQuery(id+"F16.imprint","IMPRINT",EDGE,{"derivedFrom":sQuery(id+"F16.wireOp",EDGE,"E85")}),-1.0]])]});
            var Q1;
            Q1=makeQuery(id+"F16.imprint","IMPRINT",FACE,{"disambiguationData":[TD([[makeQuery(id+"F16.imprint","IMPRINT",EDGE,{"derivedFrom":sQuery(id+"F16.wireOp",EDGE,"E79")}),-1.0]])]});
            var Q2;
            Q2=makeQuery(id+"F16.imprint","IMPRINT",FACE,{"disambiguationData":[TD([[makeQuery(id+"F16.imprint","IMPRINT",EDGE,{"derivedFrom":sQuery(id+"F16.wireOp",EDGE,"E92")}),-1.0]])]});
            var Q3;
            Q3=makeQuery(id+"F2.opExtrude","CAP_FACE",FACE,{"disambiguationData":[OSD([sQuery(id+"F0.wireOp",EDGE,"E12"),sQuery(id+"F0.wireOp",EDGE,"E13"),sQuery(id+"F0.wireOp",EDGE,"E14"),sQuery(id+"F0.wireOp",EDGE,"E15"),sQuery(id+"F0.wireOp",EDGE,"E17.filletArc"),sQuery(id+"F0.wireOp",EDGE,"E18.filletArc"),sQuery(id+"F0.wireOp",EDGE,"E19.filletArc"),sQuery(id+"F0.wireOp",EDGE,"E20.filletArc"),sQuery(id+"F0.wireOp",EDGE,"E25.0"),sQuery(id+"F0.wireOp",EDGE,"E25.1"),sQuery(id+"F0.wireOp",EDGE,"E25.2"),sQuery(id+"F0.wireOp",EDGE,"E25.3"),sQuery(id+"F0.wireOp",EDGE,"E25.4"),sQuery(id+"F0.wireOp",EDGE,"E25.5"),sQuery(id+"F0.wireOp",EDGE,"E25.6"),sQuery(id+"F0.wireOp",EDGE,"E25.7")])],"isStart":false});
            var Q4;
            Q4=makeQuery(id+"F1.opExtrude","SWEPT_BODY",BODY,{"disambiguationData":[OSD([sQuery(id+"F0.wireOp",EDGE,"E1.bottom"),sQuery(id+"F0.wireOp",EDGE,"E1.top"),sQuery(id+"F0.wireOp",EDGE,"E1.left"),sQuery(id+"F0.wireOp",EDGE,"E1.right"),sQuery(id+"F0.wireOp",EDGE,"E4"),sQuery(id+"F0.wireOp",EDGE,"E5"),sQuery(id+"F0.wireOp",EDGE,"E6"),sQuery(id+"F0.wireOp",EDGE,"E7"),sQuery(id+"F0.wireOp",EDGE,"E21.filletArc"),sQuery(id+"F0.wireOp",EDGE,"E22.filletArc"),sQuery(id+"F0.wireOp",EDGE,"E23.filletArc"),sQuery(id+"F0.wireOp",EDGE,"E24.filletArc")])]});
            extrude(context, id + "F17", {"entities" : qUnion([Q0, Q1, Q2]), "endBound" : BoundingType.UP_TO_SURFACE, "endBoundEntityFace" : qUnion([Q3]), "endBoundEntityBody" : qUnion([Q4]), "depth" : 25 * mm});
        }
    });
